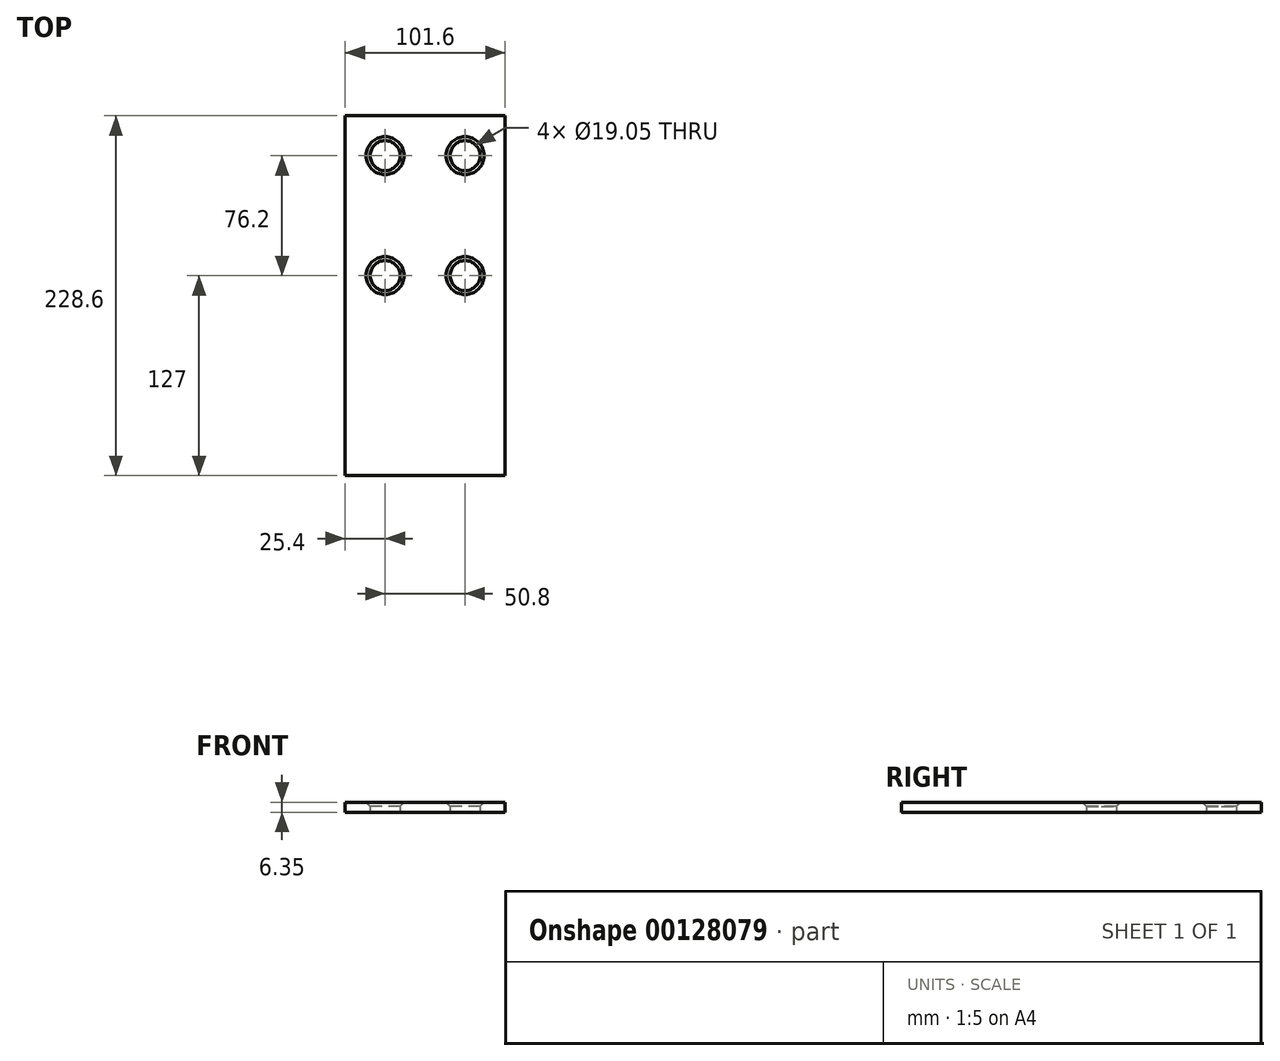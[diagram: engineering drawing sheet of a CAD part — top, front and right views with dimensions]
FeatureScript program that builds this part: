
annotation { "Feature Type Name" : "Feature", "Feature Type Description" : "" }
export const myFeature = defineFeature(function(context is Context, id is Id, definition is map)
    precondition{}
    {
        {
            var Q0;
            Q0=qCreatedBy(makeId("Top.planeOp"),FACE);
            var sketch = newSketch(context, id + "F0", { "sketchPlane" : qUnion([Q0])});
            skLineSegment(sketch, "E0", {"start": v(-50.8, 114.3) * mm, "end": v(-50.8, 0) * mm});
            skLineSegment(sketch, "E1", {"start": v(-50.8, 114.3) * mm, "end": v(50.8, 114.3) * mm});
            skLineSegment(sketch, "E2", {"start": v(50.8, 114.3) * mm, "end": v(50.8, 0) * mm});
            skLineSegment(sketch, "E3.MirrorCS", {"start": v(-50.8, -114.3) * mm, "end": v(50.8, -114.3) * mm});
            skLineSegment(sketch, "E4.MirrorCS", {"start": v(-50.8, -114.3) * mm, "end": v(-50.8, 0) * mm});
            skLineSegment(sketch, "E5.MirrorCS", {"start": v(50.8, -114.3) * mm, "end": v(50.8, 0) * mm});
            skCircle(sketch, "E6", {"center": v(-25.4, 88.9) * mm, "radius": 9.53 * mm});
            skCircle(sketch, "E7", {"center": v(25.4, 88.9) * mm, "radius": 9.53 * mm});
            skCircle(sketch, "E8", {"center": v(-25.4, 12.7) * mm, "radius": 9.53 * mm});
            skCircle(sketch, "E9", {"center": v(25.4, 12.7) * mm, "radius": 9.53 * mm});
            skSolve(sketch);
        }
        {
            var Q0;
            Q0 = qSketchRegion(id + "F0", true);
            extrude(context, id + "F1", {"entities" : qUnion([Q0]), "depth" : 6.35 * mm});
        }
        {
            var Q0;
            Q0=makeQuery(id+"F1.opExtrude","CAP_EDGE",EDGE,{"disambiguationData":[OSD([sQuery(id+"F0.wireOp",EDGE,"E6")])],"isStart":false});
            var Q1;
            Q1=makeQuery(id+"F1.opExtrude","CAP_EDGE",EDGE,{"disambiguationData":[OSD([sQuery(id+"F0.wireOp",EDGE,"E7")])],"isStart":false});
            var Q2;
            Q2=makeQuery(id+"F1.opExtrude","CAP_EDGE",EDGE,{"disambiguationData":[OSD([sQuery(id+"F0.wireOp",EDGE,"E9")])],"isStart":false});
            var Q3;
            Q3=makeQuery(id+"F1.opExtrude","CAP_EDGE",EDGE,{"disambiguationData":[OSD([sQuery(id+"F0.wireOp",EDGE,"E8")])],"isStart":false});
            chamfer(context, id + "F2", {"entities" : qUnion([Q0, Q1, Q2, Q3]), "width" : 2.54 * mm, "tangentPropagation" : true});
        }
    });
